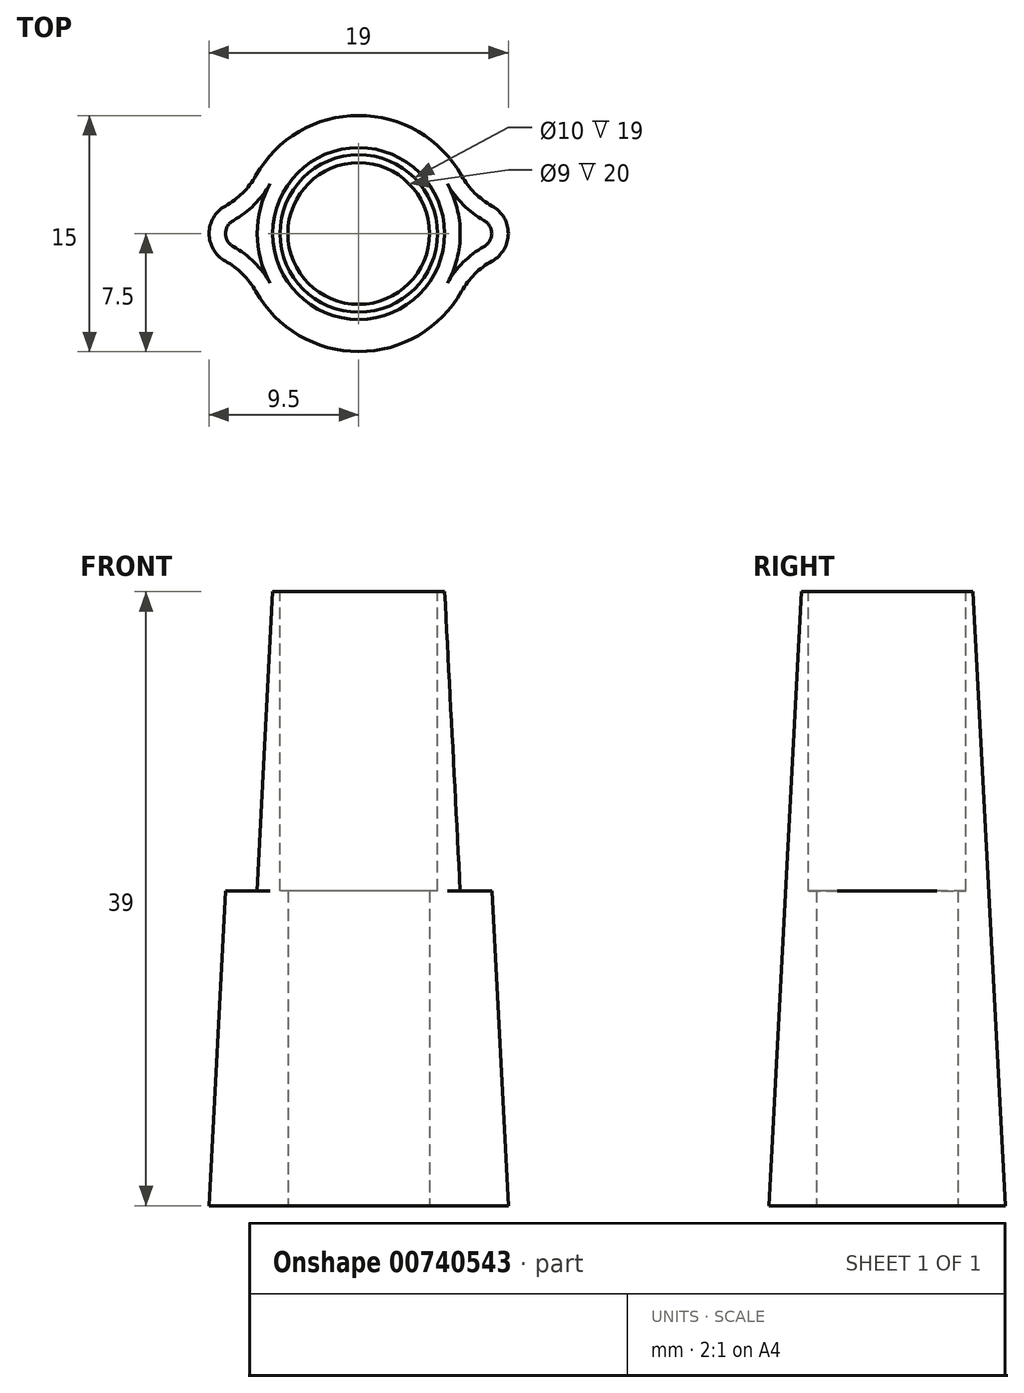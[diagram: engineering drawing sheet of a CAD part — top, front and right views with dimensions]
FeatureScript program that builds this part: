
annotation { "Feature Type Name" : "Feature", "Feature Type Description" : "" }
export const myFeature = defineFeature(function(context is Context, id is Id, definition is map)
    precondition{}
    {
        {
            var Q0;
            Q0=qCreatedBy(makeId("Top.planeOp"),FACE);
            var sketch = newSketch(context, id + "F0", { "sketchPlane" : qUnion([Q0])});
            skArc(sketch, "E0", {"start": v(-6.54, -3.67) * mm, "mid": v(0, -7.5) * mm, "end": v(6.54, -3.67) * mm});
            skArc(sketch, "E1", {"start": v(-8.47, 1.75) * mm, "mid": v(-9.5, 0) * mm, "end": v(-8.47, -1.75) * mm});
            skArc(sketch, "E2", {"start": v(8.47, -1.75) * mm, "mid": v(9.5, 0) * mm, "end": v(8.47, 1.75) * mm});
            skArc(sketch, "E3.trimOffspring", {"start": v(6.54, 3.67) * mm, "mid": v(0, 7.5) * mm, "end": v(-6.54, 3.67) * mm});
            skPoint(sketch, "E4.visualSharp", {"position": v(-7.23, 1.98) * mm});
            skArc(sketch, "E4.filletArc", {"start": v(-8.47, 1.75) * mm, "mid": v(-7.37, 2.58) * mm, "end": v(-6.54, 3.67) * mm});
            skPoint(sketch, "E5.visualSharp", {"position": v(-7.23, -1.98) * mm});
            skArc(sketch, "E5.filletArc", {"start": v(-6.54, -3.67) * mm, "mid": v(-7.37, -2.58) * mm, "end": v(-8.47, -1.75) * mm});
            skPoint(sketch, "E6.visualSharp", {"position": v(7.23, 1.98) * mm});
            skArc(sketch, "E6.filletArc", {"start": v(6.54, 3.67) * mm, "mid": v(7.37, 2.58) * mm, "end": v(8.47, 1.75) * mm});
            skPoint(sketch, "E7.visualSharp", {"position": v(7.23, -1.98) * mm});
            skArc(sketch, "E7.filletArc", {"start": v(8.47, -1.75) * mm, "mid": v(7.37, -2.58) * mm, "end": v(6.54, -3.67) * mm});
            skSolve(sketch);
        }
        {
            var Q0;
            Q0=makeQuery(id+"F0.imprint","IMPRINT",FACE,{"disambiguationData":[TD([[makeQuery(id+"F0.imprint","IMPRINT",EDGE,{"derivedFrom":sQuery(id+"F0.wireOp",EDGE,"E0")}),1.0]])]});
            extrude(context, id + "F1", {"entities" : qUnion([Q0]), "depth" : 20 * mm, "offsetDistance" : 25 * mm, "hasDraft" : true, "draftAngle" : 3 * degree, "draftPullDirection" : true});
        }
        {
            var Q0;
            Q0=makeQuery(id+"F1.opExtrude","CAP_FACE",FACE,{"disambiguationData":[OSD([sQuery(id+"F0.wireOp",EDGE,"E0"),sQuery(id+"F0.wireOp",EDGE,"E1"),sQuery(id+"F0.wireOp",EDGE,"E2"),sQuery(id+"F0.wireOp",EDGE,"E3.trimOffspring"),sQuery(id+"F0.wireOp",EDGE,"E4.filletArc"),sQuery(id+"F0.wireOp",EDGE,"E5.filletArc"),sQuery(id+"F0.wireOp",EDGE,"E6.filletArc"),sQuery(id+"F0.wireOp",EDGE,"E7.filletArc")])],"isStart":false});
            var sketch = newSketch(context, id + "F2", { "sketchPlane" : qUnion([Q0])});
            skArc(sketch, "E8.0", {"start": v(-5.63, -3.16) * mm, "mid": v(0, -6.45) * mm, "end": v(5.63, -3.16) * mm});
            skArc(sketch, "E9.0", {"start": v(5.63, 3.16) * mm, "mid": v(0, 6.45) * mm, "end": v(-5.63, 3.16) * mm});
            skArc(sketch, "E10", {"start": v(-5.63, 3.16) * mm, "mid": v(-6.45, 0) * mm, "end": v(-5.63, -3.16) * mm});
            skArc(sketch, "E11", {"start": v(5.63, 3.16) * mm, "mid": v(6.45, 0) * mm, "end": v(5.63, -3.16) * mm});
            skSolve(sketch);
        }
        {
            var Q0;
            Q0=makeQuery(id+"F2.imprint","IMPRINT",FACE,{"disambiguationData":[TD([[makeQuery(id+"F2.imprint","IMPRINT",EDGE,{"derivedFrom":sQuery(id+"F2.wireOp",EDGE,"E8.0")}),1.0]])]});
            extrude(context, id + "F3", {"entities" : qUnion([Q0]), "operationType" : NewBodyOperationType.ADD, "depth" : 19 * mm, "offsetDistance" : 25 * mm, "hasDraft" : true, "draftAngle" : 3 * degree, "draftPullDirection" : true});
        }
        {
            var Q0;
            Q0=makeQuery(id+"F3.opExtrude","CAP_FACE",FACE,{"disambiguationData":[OSD([sQuery(id+"F2.wireOp",EDGE,"E8.0"),sQuery(id+"F2.wireOp",EDGE,"E9.0"),sQuery(id+"F2.wireOp",EDGE,"E10"),sQuery(id+"F2.wireOp",EDGE,"E11")])],"isStart":false});
            var sketch = newSketch(context, id + "F4", { "sketchPlane" : qUnion([Q0])});
            skCircle(sketch, "E12", {"center": v(0, 0) * mm, "radius": 5 * mm});
            skSolve(sketch);
        }
        {
            var Q0;
            Q0 = qSketchRegion(id + "F4", true);
            extrude(context, id + "F5", {"entities" : qUnion([Q0]), "operationType" : NewBodyOperationType.REMOVE, "oppositeDirection" : true, "depth" : 19 * mm, "offsetDistance" : 25 * mm});
        }
        {
            var Q0;
            Q0=makeQuery(id+"F1.opExtrude","CAP_FACE",FACE,{"disambiguationData":[OSD([sQuery(id+"F0.wireOp",EDGE,"E0"),sQuery(id+"F0.wireOp",EDGE,"E1"),sQuery(id+"F0.wireOp",EDGE,"E2"),sQuery(id+"F0.wireOp",EDGE,"E3.trimOffspring"),sQuery(id+"F0.wireOp",EDGE,"E4.filletArc"),sQuery(id+"F0.wireOp",EDGE,"E5.filletArc"),sQuery(id+"F0.wireOp",EDGE,"E6.filletArc"),sQuery(id+"F0.wireOp",EDGE,"E7.filletArc")])],"isStart":true});
            var sketch = newSketch(context, id + "F6", { "sketchPlane" : qUnion([Q0])});
            skCircle(sketch, "E13", {"center": v(0, 0) * mm, "radius": 4.5 * mm});
            skSolve(sketch);
        }
        {
            var Q0;
            Q0=makeQuery(id+"F6.imprint","IMPRINT",FACE,{"disambiguationData":[TD([[makeQuery(id+"F6.imprint","IMPRINT",EDGE,{"derivedFrom":sQuery(id+"F6.wireOp",EDGE,"E13")}),1.0]])]});
            extrude(context, id + "F7", {"entities" : qUnion([Q0]), "operationType" : NewBodyOperationType.REMOVE, "endBound" : BoundingType.UP_TO_NEXT, "oppositeDirection" : true, "depth" : 25 * mm, "offsetDistance" : 25 * mm});
        }
    });
